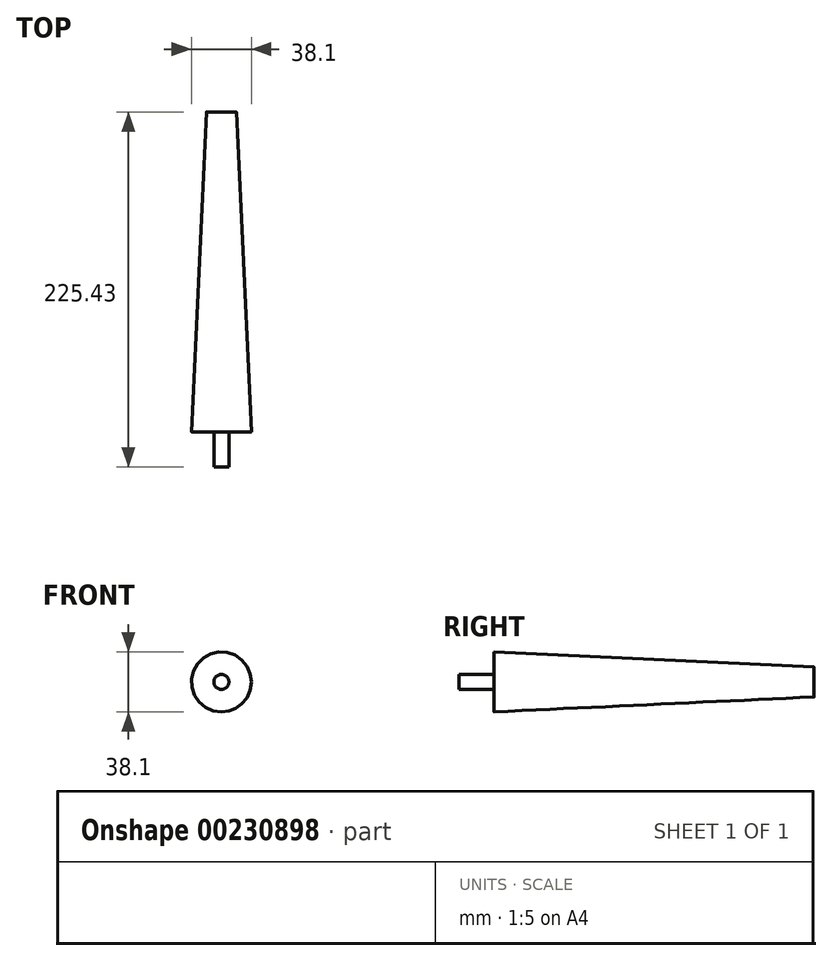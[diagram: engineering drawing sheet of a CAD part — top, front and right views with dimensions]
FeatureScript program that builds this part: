
annotation { "Feature Type Name" : "Feature", "Feature Type Description" : "" }
export const myFeature = defineFeature(function(context is Context, id is Id, definition is map)
    precondition{}
    {
        {
            var Q0;
            Q0=qCreatedBy(makeId("Front.planeOp"),FACE);
            var sketch = newSketch(context, id + "F0", { "sketchPlane" : qUnion([Q0])});
            skCircle(sketch, "E0", {"center": v(0, 0) * mm, "radius": 9.53 * mm});
            skSolve(sketch);
        }
        {
            var Q0;
            Q0=qCreatedBy(makeId("Front.planeOp"),FACE);
            cPlane(context, id + "F1", {"entities" : qUnion([Q0]), "cplaneType" : CPlaneType.OFFSET, "offset" : 203.2 * mm, "width" : 152.4 * mm, "height" : 152.4 * mm});
        }
        {
            var Q0;
            Q0=qCreatedBy(id+"F1.planeOp",FACE);
            var sketch = newSketch(context, id + "F2", { "sketchPlane" : qUnion([Q0])});
            skPoint(sketch, "E1.0", {"position": v(0, 0) * mm});
            skCircle(sketch, "E2", {"center": v(0, 0) * mm, "radius": 19.05 * mm});
            skSolve(sketch);
        }
        {
            var Q0;
            Q0=makeQuery(id+"F0.imprint","IMPRINT",FACE,{"disambiguationData":[TD([[makeQuery(id+"F0.imprint","IMPRINT",EDGE,{"derivedFrom":sQuery(id+"F0.wireOp",EDGE,"E0")}),1.0]])]});
            var Q1;
            Q1=makeQuery(id+"F2.imprint","IMPRINT",FACE,{"disambiguationData":[TD([[makeQuery(id+"F2.imprint","IMPRINT",EDGE,{"derivedFrom":sQuery(id+"F2.wireOp",EDGE,"E2")}),1.0]])]});
            loft(context, id + "F3", {"sheetProfilesArray" : [{ "sheetProfileEntities" : qUnion([Q0]) }, { "sheetProfileEntities" : qUnion([Q1]) }]});
        }
        {
            var Q0;
            Q0=qCreatedBy(id+"F1.planeOp",FACE);
            var sketch = newSketch(context, id + "F4", { "sketchPlane" : qUnion([Q0])});
            skCircle(sketch, "E3", {"center": v(0, 0) * mm, "radius": 4.76 * mm});
            skSolve(sketch);
        }
        {
            var Q0;
            Q0 = qSketchRegion(id + "F4", true);
            extrude(context, id + "F5", {"entities" : qUnion([Q0]), "operationType" : NewBodyOperationType.ADD, "depth" : 22.22 * mm});
        }
        {
            assignVariable(context, id + "F6", {"name" : "edgeChamfer", "anyValue" : 1 / 16});
        }
        {
            var Q0;
            Q0=makeQuery(id+"F3.opLoft","MID_CAP_EDGE",EDGE,{"disambiguationData":[OSD([sQuery(id+"F0.wireOp",EDGE,"E0")])],"capPos":0.0});
            fillet(context, id + "F7", {"entities" : qUnion([Q0]), "radius" : (getVariable(context, 'edgeChamfer')) * mm, "tangentPropagation" : true, "allowEdgeOverflow" : false});
        }
        {
            var Q0;
            Q0=makeQuery(id+"F3.opLoft","MID_CAP_EDGE",EDGE,{"disambiguationData":[OSD([sQuery(id+"F0.wireOp",EDGE,"E0"),sQuery(id+"F2.wireOp",EDGE,"E2")])],"capPos":1.0});
            fillet(context, id + "F8", {"entities" : qUnion([Q0]), "radius" : (getVariable(context, 'edgeChamfer')) * mm, "tangentPropagation" : true, "allowEdgeOverflow" : false});
        }
    });
